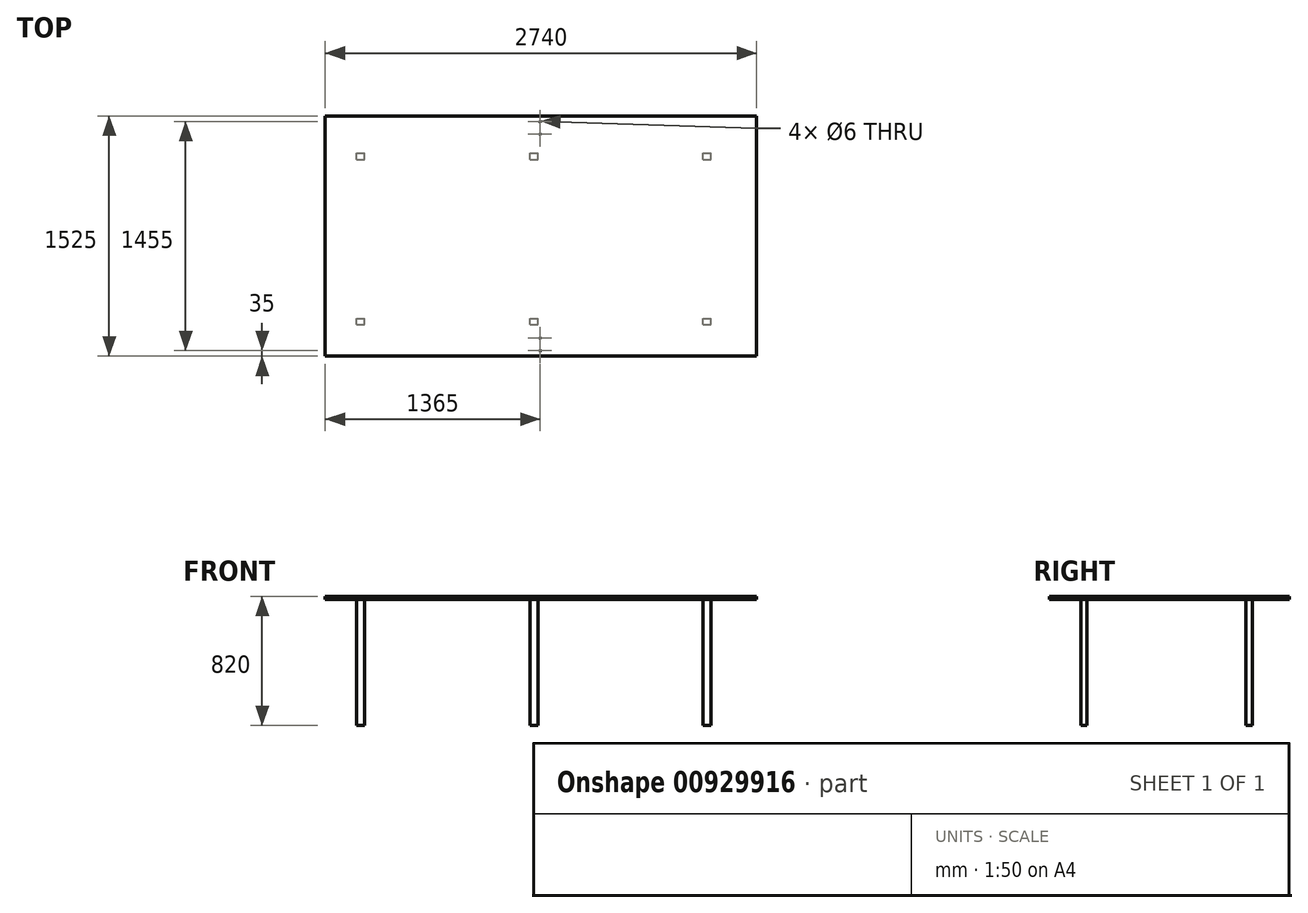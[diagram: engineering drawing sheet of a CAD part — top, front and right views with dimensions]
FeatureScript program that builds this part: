
annotation { "Feature Type Name" : "Feature", "Feature Type Description" : "" }
export const myFeature = defineFeature(function(context is Context, id is Id, definition is map)
    precondition{}
    {
        {
            var Q0;
            Q0=qCreatedBy(makeId("Top.planeOp"),FACE);
            var sketch = newSketch(context, id + "F0", { "sketchPlane" : qUnion([Q0])});
            skLineSegment(sketch, "E0.bottom", {"start": v(0, 0) * mm, "end": v(2740, 0) * mm});
            skLineSegment(sketch, "E0.top", {"start": v(0, 1525) * mm, "end": v(2740, 1525) * mm});
            skLineSegment(sketch, "E0.left", {"start": v(0, 0) * mm, "end": v(0, 1525) * mm});
            skLineSegment(sketch, "E0.right", {"start": v(2740, 0) * mm, "end": v(2740, 1525) * mm});
            skSolve(sketch);
        }
        {
            var Q0;
            Q0=makeQuery(id+"F0.imprint","IMPRINT",FACE,{"disambiguationData":[TD([[makeQuery(id+"F0.imprint","IMPRINT",EDGE,{"derivedFrom":sQuery(id+"F0.wireOp",EDGE,"E0.bottom")}),1.0]])]});
            extrude(context, id + "F1", {"entities" : qUnion([Q0]), "depth" : 20 * mm, "offsetDistance" : 25 * mm});
        }
        {
            var Q0;
            Q0=makeQuery(id+"F1.opExtrude","CAP_FACE",FACE,{"disambiguationData":[OSD([sQuery(id+"F0.wireOp",EDGE,"E0.bottom"),sQuery(id+"F0.wireOp",EDGE,"E0.top"),sQuery(id+"F0.wireOp",EDGE,"E0.left"),sQuery(id+"F0.wireOp",EDGE,"E0.right")])],"isStart":false});
            var sketch = newSketch(context, id + "F2", { "sketchPlane" : qUnion([Q0])});
            skLineSegment(sketch, "E1", {"start": v(1365, 1525) * mm, "end": v(1365, 0) * mm, "construction": true});
            skPoint(sketch, "E1.endSnap0", {"position": v(1370, 0) * mm});
            skCircle(sketch, "E2", {"center": v(1365, 1490) * mm, "radius": 3 * mm});
            skCircle(sketch, "E3", {"center": v(1365, 1410) * mm, "radius": 3 * mm});
            skCircle(sketch, "E4", {"center": v(1365, 35) * mm, "radius": 3 * mm});
            skCircle(sketch, "E5", {"center": v(1365, 115) * mm, "radius": 3 * mm});
            skSolve(sketch);
        }
        {
            var Q0;
            Q0 = qSketchRegion(id + "F2", true);
            extrude(context, id + "F3", {"entities" : qUnion([Q0]), "operationType" : NewBodyOperationType.REMOVE, "oppositeDirection" : true, "depth" : 25 * mm, "offsetDistance" : 25 * mm});
        }
        {
            var Q0;
            Q0=makeQuery(id+"F1.opExtrude","CAP_FACE",FACE,{"disambiguationData":[OSD([sQuery(id+"F0.wireOp",EDGE,"E0.bottom"),sQuery(id+"F0.wireOp",EDGE,"E0.top"),sQuery(id+"F0.wireOp",EDGE,"E0.left"),sQuery(id+"F0.wireOp",EDGE,"E0.right")])],"isStart":true});
            var sketch = newSketch(context, id + "F4", { "sketchPlane" : qUnion([Q0])});
            skLineSegment(sketch, "E6.bottom", {"start": v(200, -200) * mm, "end": v(250, -200) * mm});
            skLineSegment(sketch, "E6.top", {"start": v(200, -240) * mm, "end": v(250, -240) * mm});
            skLineSegment(sketch, "E6.left", {"start": v(200, -200) * mm, "end": v(200, -240) * mm});
            skLineSegment(sketch, "E6.right", {"start": v(250, -200) * mm, "end": v(250, -240) * mm});
            skLineSegment(sketch, "E7.0.1.0", {"start": v(250, -1250) * mm, "end": v(250, -1290) * mm});
            skLineSegment(sketch, "E7.0.1.1", {"start": v(200, -1250) * mm, "end": v(200, -1290) * mm});
            skLineSegment(sketch, "E7.0.1.2", {"start": v(200, -1290) * mm, "end": v(250, -1290) * mm});
            skLineSegment(sketch, "E7.0.1.3", {"start": v(200, -1250) * mm, "end": v(250, -1250) * mm});
            skLineSegment(sketch, "E7.1.0.0", {"start": v(1350, -200) * mm, "end": v(1350, -240) * mm});
            skLineSegment(sketch, "E7.1.0.1", {"start": v(1300, -200) * mm, "end": v(1300, -240) * mm});
            skLineSegment(sketch, "E7.1.0.2", {"start": v(1300, -240) * mm, "end": v(1350, -240) * mm});
            skLineSegment(sketch, "E7.1.0.3", {"start": v(1300, -200) * mm, "end": v(1350, -200) * mm});
            skLineSegment(sketch, "E7.1.1.0", {"start": v(1350, -1250) * mm, "end": v(1350, -1290) * mm});
            skLineSegment(sketch, "E7.1.1.1", {"start": v(1300, -1250) * mm, "end": v(1300, -1290) * mm});
            skLineSegment(sketch, "E7.1.1.2", {"start": v(1300, -1290) * mm, "end": v(1350, -1290) * mm});
            skLineSegment(sketch, "E7.1.1.3", {"start": v(1300, -1250) * mm, "end": v(1350, -1250) * mm});
            skLineSegment(sketch, "E7.2.0.0", {"start": v(2450, -200) * mm, "end": v(2450, -240) * mm});
            skLineSegment(sketch, "E7.2.0.1", {"start": v(2400, -200) * mm, "end": v(2400, -240) * mm});
            skLineSegment(sketch, "E7.2.0.2", {"start": v(2400, -240) * mm, "end": v(2450, -240) * mm});
            skLineSegment(sketch, "E7.2.0.3", {"start": v(2400, -200) * mm, "end": v(2450, -200) * mm});
            skLineSegment(sketch, "E7.2.1.0", {"start": v(2450, -1250) * mm, "end": v(2450, -1290) * mm});
            skLineSegment(sketch, "E7.2.1.1", {"start": v(2400, -1250) * mm, "end": v(2400, -1290) * mm});
            skLineSegment(sketch, "E7.2.1.2", {"start": v(2400, -1290) * mm, "end": v(2450, -1290) * mm});
            skLineSegment(sketch, "E7.2.1.3", {"start": v(2400, -1250) * mm, "end": v(2450, -1250) * mm});
            skLineSegment(sketch, "E7.direction1", {"start": v(200, -240) * mm, "end": v(1300, -240) * mm, "construction": true});
            skLineSegment(sketch, "E7.direction2", {"start": v(200, -240) * mm, "end": v(200, -1290) * mm, "construction": true});
            skSolve(sketch);
        }
        {
            var Q0;
            Q0 = qSketchRegion(id + "F4", true);
            extrude(context, id + "F5", {"entities" : qUnion([Q0]), "operationType" : NewBodyOperationType.ADD, "depth" : 800 * mm, "offsetDistance" : 25 * mm});
        }
    });
